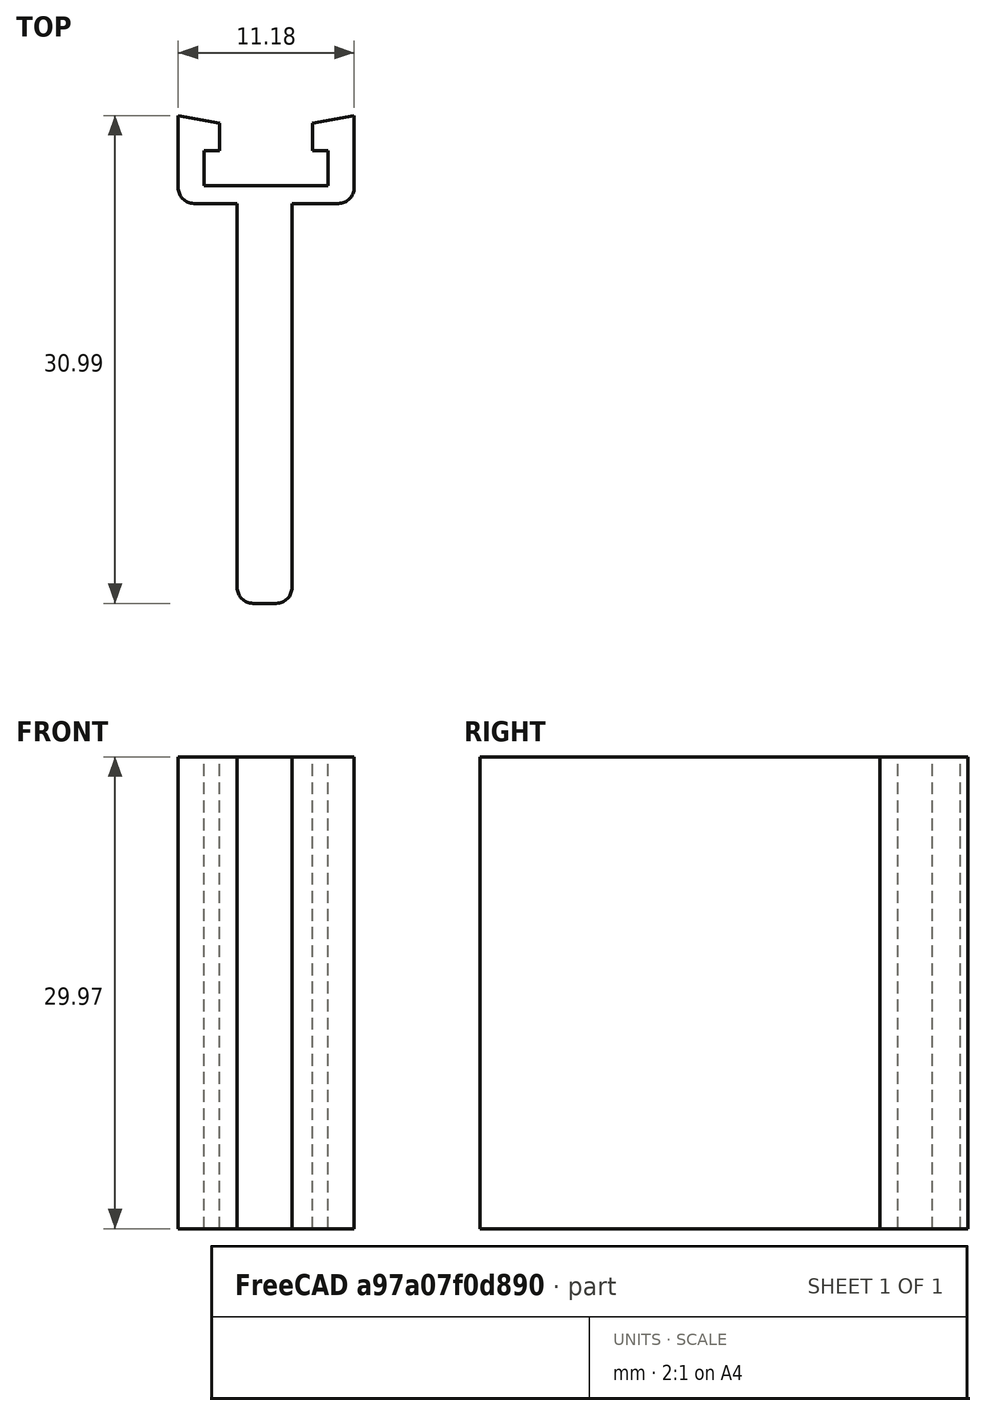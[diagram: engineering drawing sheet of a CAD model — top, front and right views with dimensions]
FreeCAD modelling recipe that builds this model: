
FCSTD DOCUMENT  (FreeCAD 0.18R4 (GitTag))
Label: BlindsTab
License: All rights reserved
LicenseURL: http://en.wikipedia.org/wiki/All_rights_reserved
objects: Sketcher::SketchObject×2, PartDesign::Pad×2, PartDesign::Fillet×1, PartDesign::Body×1, Mesh::Feature×1
note: 8 computed .brp shape members not serialized (recipe doc carries the construction recipe); baked Part::Feature solids carry a one-line shape summary decoded from their .brp

FEATURE [Sketcher::SketchObject] Sketch
  MapMode = 5
  Support = -> [XY_Plane]
  sketch-geometry (16):
    g0: LineSegment StartX=0 StartY=0 StartZ=0 EndX=11.176 EndY=0 EndZ=0
    g1: LineSegment StartX=11.176 StartY=0 StartZ=0 EndX=11.176 EndY=5.588 EndZ=0
    g2: LineSegment StartX=0 StartY=5.588 StartZ=0 EndX=0 EndY=0 EndZ=0
    g3: LineSegment StartX=8.5471 StartY=5.088 StartZ=0 EndX=8.5471 EndY=3.338 EndZ=0
    g4: LineSegment StartX=2.6289 StartY=3.338 StartZ=0 EndX=2.6289 EndY=5.088 EndZ=0
    g5: LineSegment StartX=9.525 StartY=3.338 StartZ=0 EndX=9.525 EndY=1.138 EndZ=0
    g6: LineSegment StartX=9.525 StartY=1.138 StartZ=0 EndX=1.651 EndY=1.138 EndZ=0
    g7: LineSegment StartX=1.651 StartY=1.138 StartZ=0 EndX=1.651 EndY=3.338 EndZ=0
    g8: LineSegment StartX=0 StartY=5.588 StartZ=0 EndX=2.6289 EndY=5.088 EndZ=0
    g9: LineSegment StartX=8.5471 StartY=5.088 StartZ=0 EndX=11.176 EndY=5.588 EndZ=0
    g10: LineSegment StartX=1.651 StartY=3.338 StartZ=0 EndX=2.6289 EndY=3.338 EndZ=0
    g11: LineSegment StartX=8.5471 StartY=3.338 StartZ=0 EndX=9.525 EndY=3.338 EndZ=0
    g12: LineSegment [constr] StartX=2.6289 StartY=5.088 StartZ=0 EndX=8.5471 EndY=5.088 EndZ=0
    g13: GeomPoint X=5.588 Y=0 Z=0
    g14: GeomPoint X=5.588 Y=5.588 Z=0
    g15: LineSegment [constr] StartX=5.588 StartY=5.588 StartZ=0 EndX=5.588 EndY=0 EndZ=0
  constraints (39):
    c: Coincident(g0,g1)
    c: Coincident(g2,g0)
    c: Horizontal(g0)
    c: Vertical(g1)
    c: Vertical(g2)
    c: Vertical(g3)
    c: Vertical(g4)
    c: Coincident(g5,g6)
    c: Coincident(g6,g7)
    c: Vertical(g5)
    c: Vertical(g7)
    c: Coincident(g11,g5)
    c: Coincident(g3,g9)
    c: Coincident(g11,g3)
    c: Coincident(g1,g9)
    c: Coincident(g8,g4)
    c: Coincident(g10,g4)
    c: Coincident(g10,g7)
    c: Coincident(g8,g2)
    c: Coincident(g0,g-1)
    c: Equal(g2,g1)
    c: Distance(g2) = 5.588
    c: Distance(g0) = 11.176
    c: Distance(g6) = 7.874
    c: Coincident(g12,g4)
    c: Coincident(g12,g3)
    c: Distance(g12) = 5.9182
    c: Symmetric(g2,g1,g14)
    c: Symmetric(g0,g0,g13)
    c: Coincident(g13,g15)
    c: Coincident(g14,g15)
    c: Symmetric(g4,g3,g15)
    c: Symmetric(g6,g5,g15)
    c: Distance(g3,g6) = 3.95
    c: Distance(g3,g12) = 1.75
    c: Parallel(g10,g0)
    c: Parallel(g11,g0)
    c: Parallel(g12,g0)
    c: Distance(g2,g12) = 0.5
FEATURE [PartDesign::Pad] Pad
  Length = 29.972
  Length2 = 100
  Profile = -> Sketch
  Type = 0
FEATURE [Sketcher::SketchObject] Sketch001
  ExternalGeometry = -> [Pad]
  MapMode = 5
  Placement = pos=(0,0,0) rot=(1,0,0;1.5708rad)
  Support = -> [Pad]
  sketch-geometry (4):
    g0: LineSegment StartX=3.75 StartY=29.972 StartZ=0 EndX=7.23 EndY=29.972 EndZ=0
    g1: LineSegment StartX=7.23 StartY=29.972 StartZ=0 EndX=7.23 EndY=0 EndZ=0
    g2: LineSegment StartX=7.23 StartY=0 StartZ=0 EndX=3.75 EndY=0 EndZ=0
    g3: LineSegment StartX=3.75 StartY=0 StartZ=0 EndX=3.75 EndY=29.972 EndZ=0
  constraints (12):
    c: Coincident(g0,g1)
    c: Coincident(g1,g2)
    c: Coincident(g2,g3)
    c: Coincident(g3,g0)
    c: Horizontal(g0)
    c: Horizontal(g2)
    c: Vertical(g1)
    c: Vertical(g3)
    c: Distance(g2) = 3.48
    c: Distance(g2,g-3) = 3.75
    c: PointOnObject(g2,g-5)
    c: PointOnObject(g0,g-4)
FEATURE [PartDesign::Pad] Pad001
  BaseFeature = -> Pad
  Length = 25.4
  Length2 = 100
  Profile = -> Sketch001
  Type = 0
FEATURE [PartDesign::Fillet] Fillet
  Base = -> Pad001 [Edge49,Edge50,Edge33,Edge40]
  BaseFeature = -> Pad001
  Radius = 1
FEATURE [PartDesign::Body] Body
  Group = -> [Sketch,Pad,Sketch001,Pad001,Fillet]
  Origin = -> Origin
  Tip = -> Fillet
FEATURE [Mesh::Feature] Mesh  label="Body (Meshed)"
